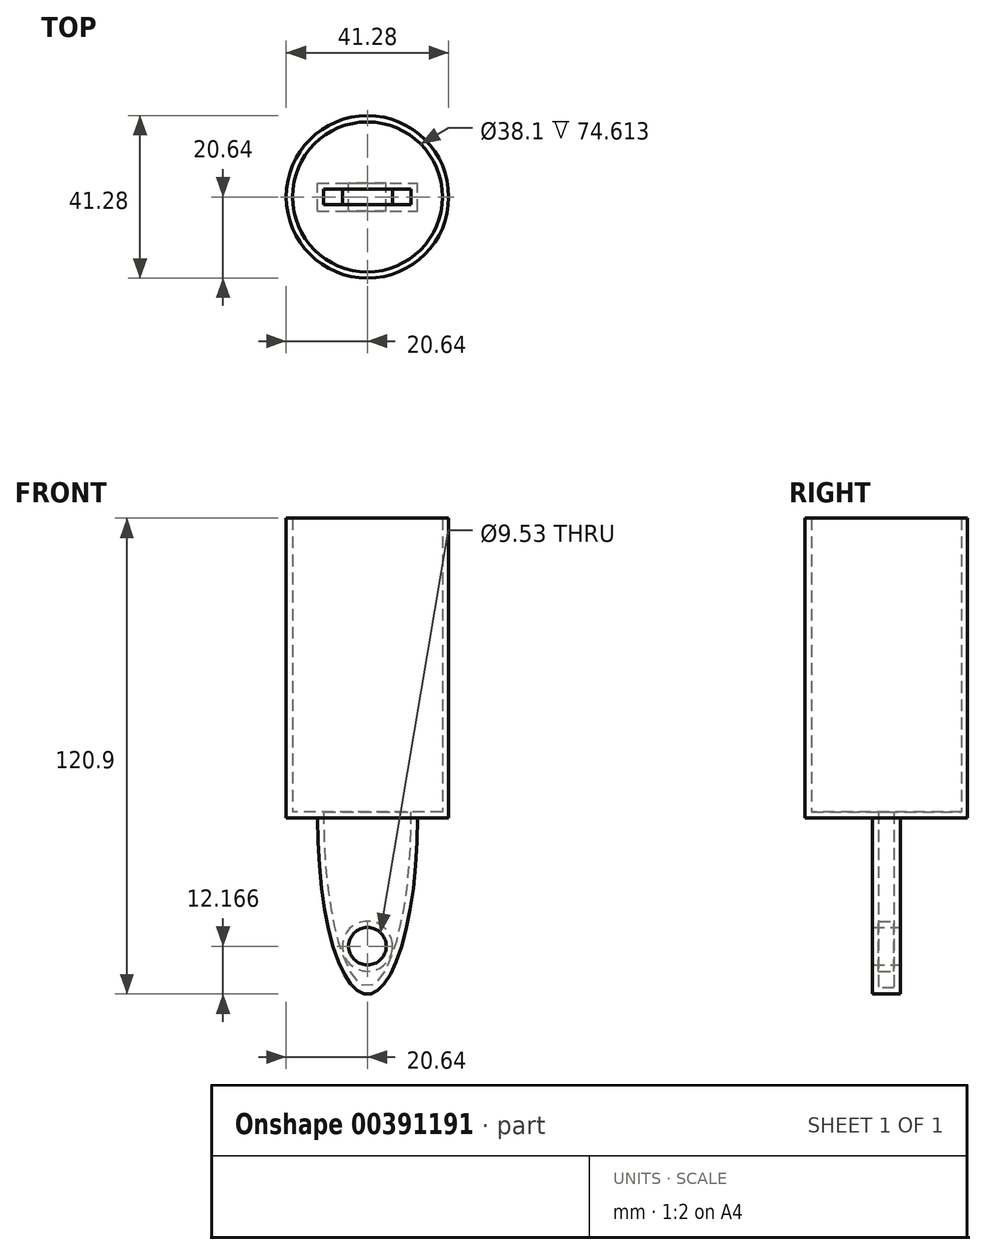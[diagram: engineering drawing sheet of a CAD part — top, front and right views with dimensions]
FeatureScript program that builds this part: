
annotation { "Feature Type Name" : "Feature", "Feature Type Description" : "" }
export const myFeature = defineFeature(function(context is Context, id is Id, definition is map)
    precondition{}
    {
        {
            var Q0;
            Q0=qCreatedBy(makeId("Front.planeOp"),FACE);
            var sketch = newSketch(context, id + "F0", { "sketchPlane" : qUnion([Q0])});
            skCircle(sketch, "E0", {"center": v(0, -12.84) * mm, "radius": 4.76 * mm});
            skEllipticalArc(sketch, "E1", {});
            skLineSegment(sketch, "E2", {"start": v(-12.7, 19.69) * mm, "end": v(12.7, 19.69) * mm});
            skLineSegment(sketch, "E3", {"start": v(0, 19.69) * mm, "end": v(0, -25) * mm, "construction": true});
            const initialGuessF0  = {"E1": [1.694662188356233e-09, 0.019685674105118046, 0, -1, 0.044693825766444206, 0.0127, 4.71238898038469, 1.5707963267948966]};
            skSetInitialGuess(sketch, initialGuessF0);
            skSolve(sketch);
        }
        {
            var Q0;
            Q0=sQuery(id+"F0.wireOp",VERTEX,"E1.center");
            var Q1;
            Q1=qCreatedBy(makeId("Top.planeOp"),FACE);
            cPlane(context, id + "F1", {"entities" : qUnion([Q0, Q1]), "cplaneType" : CPlaneType.PLANE_POINT, "offset" : 25.4 * mm, "width" : 152.4 * mm, "height" : 152.4 * mm});
        }
        {
            var Q0;
            Q0=qCreatedBy(id+"F1.planeOp",FACE);
            var sketch = newSketch(context, id + "F2", { "sketchPlane" : qUnion([Q0])});
            skCircle(sketch, "E4", {"center": v(0, 0) * mm, "radius": 20.64 * mm});
            skSolve(sketch);
        }
        {
            var Q0;
            Q0=makeQuery(id+"F2.imprint","IMPRINT",FACE,{"disambiguationData":[TD([[makeQuery(id+"F2.imprint","IMPRINT",EDGE,{"derivedFrom":sQuery(id+"F2.wireOp",EDGE,"E4")}),1.0]])]});
            extrude(context, id + "F3", {"entities" : qUnion([Q0]), "depth" : 76.2 * mm});
        }
        {
            var Q0;
            Q0=makeQuery(id+"F0.imprint","IMPRINT",FACE,{"disambiguationData":[TD([[makeQuery(id+"F0.imprint","IMPRINT",EDGE,{"derivedFrom":sQuery(id+"F0.wireOp",EDGE,"E0")}),-1.0]])]});
            extrude(context, id + "F4", {"entities" : qUnion([Q0]), "operationType" : NewBodyOperationType.ADD, "depth" : 7.11 * mm, "symmetric" : true});
        }
        {
            var Q0;
            Q0=makeQuery(id+"F3.opExtrude","CAP_FACE",FACE,{"disambiguationData":[OSD([sQuery(id+"F2.wireOp",EDGE,"E4")])],"isStart":false});
            shell(context, id + "F5", {"entities" : qUnion([Q0]), "thickness" : 1.59 * mm});
        }
    });
